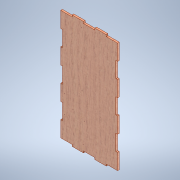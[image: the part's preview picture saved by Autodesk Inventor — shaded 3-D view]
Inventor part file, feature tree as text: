
AUTODESK INVENTOR PART (.ipt)
format: ipt  version: 2020.3 (Build 243373000, 373)  size: 178,688 bytes
history: native  units: mm
features: other x1, extrude x1, sketch x1
ambient origin geometry x8: Origin, YZ Plane, XZ Plane, XY Plane, X Axis, Y Axis, Z Axis, Center Point
bodies: Body1 (feature_tree)
feature tree (3):
  other  "Sólido1"
  extrude  "Extrusión1"  Depth=27.71mm
  sketch  "Boceto1"  dims[d0=3.0mm d1=27.71mm d2=3.0mm d3=27.72mm d4=3.0mm d5=27.71mm d6=3.0mm d7=27.72mm d8=3.0mm d9=27.71mm d10=3.0mm d11=27.72mm d12=3.0mm d13=27.71mm d14=20.0mm d16=20.0mm d18=20.0mm d20=20.0mm d22=20.0mm d23=27.71mm d24=3.0mm d25=27.72mm d26=3.0mm d27=27.71mm d28=3.0mm d29=27.72mm d30=3.0mm d31=27.71mm d32=3.0mm d33=27.72mm d34=3.0mm d35=20.0mm d39=20.0mm d41=3.0mm d42=0.0mm d46=3.0mm d47=27.71mm d50=3.0mm]
